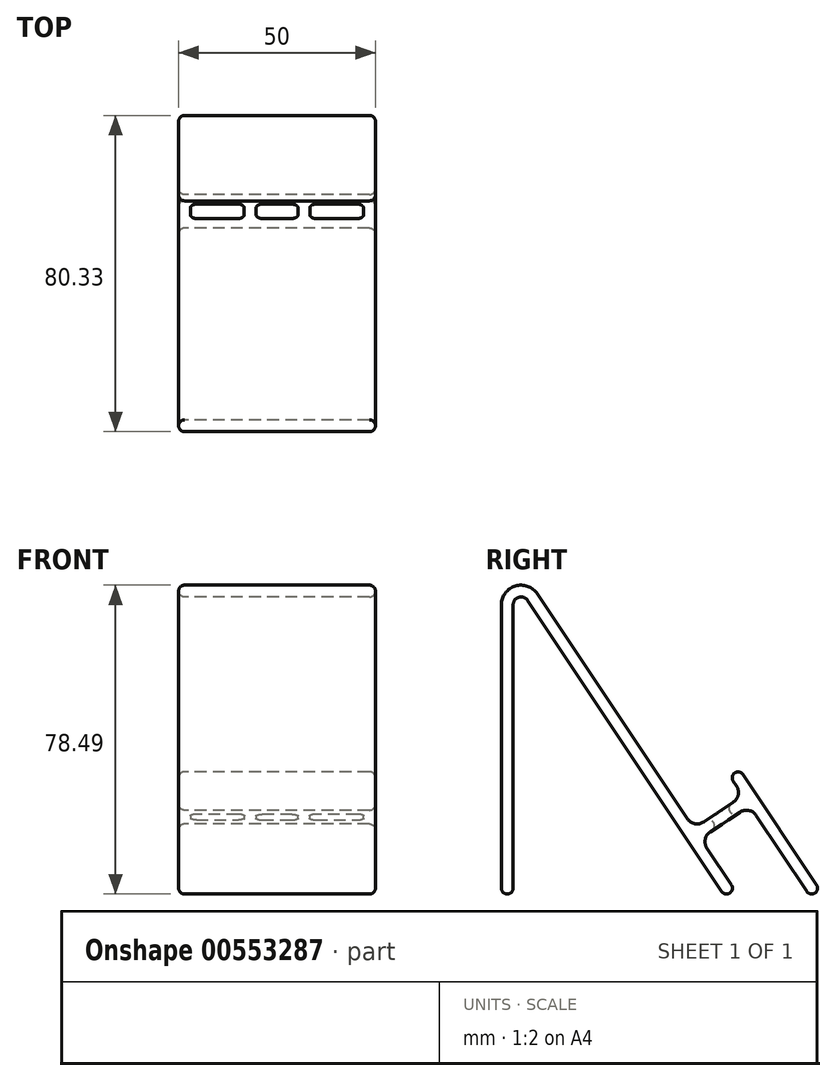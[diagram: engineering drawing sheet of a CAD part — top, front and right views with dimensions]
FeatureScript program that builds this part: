
annotation { "Feature Type Name" : "Feature", "Feature Type Description" : "" }
export const myFeature = defineFeature(function(context is Context, id is Id, definition is map)
    precondition{}
    {
        {
            var Q0;
            Q0=qCreatedBy(makeId("Right.planeOp"),FACE);
            var sketch = newSketch(context, id + "F0", { "sketchPlane" : qUnion([Q0])});
            skLineSegment(sketch, "E0", {"start": v(0, 0) * mm, "end": v(-3.6, 0) * mm});
            skLineSegment(sketch, "E1", {"start": v(-60, 0) * mm, "end": v(-60, 73.49) * mm});
            skLineSegment(sketch, "E2", {"start": v(-50.84, 76.26) * mm, "end": v(-12.76, 19.14) * mm});
            skLineSegment(sketch, "E3", {"start": v(-8.6, 18.3) * mm, "end": v(-1.1, 23.3) * mm});
            skLineSegment(sketch, "E4", {"start": v(-0.28, 27.46) * mm, "end": v(-1.1, 28.7) * mm});
            skLineSegment(sketch, "E5", {"start": v(-0.7, 30.79) * mm, "end": v(-0.7, 30.79) * mm});
            skLineSegment(sketch, "E6", {"start": v(1.39, 30.37) * mm, "end": v(21.63, 0) * mm});
            skLineSegment(sketch, "E7", {"start": v(21.63, 0) * mm, "end": v(18.03, 0) * mm});
            skPoint(sketch, "E8.visualSharp", {"position": v(-60, 90) * mm});
            skArc(sketch, "E8.filletArc", {"start": v(-50.84, 76.26) * mm, "mid": v(-56.45, 78.27) * mm, "end": v(-60, 73.49) * mm});
            skLineSegment(sketch, "E9.0", {"start": v(-53.34, 74.6) * mm, "end": v(-3.6, 0) * mm});
            skArc(sketch, "E9.1", {"start": v(-53.34, 74.6) * mm, "mid": v(-55.58, 75.4) * mm, "end": v(-57, 73.49) * mm});
            skLineSegment(sketch, "E9.2", {"start": v(-57, 0) * mm, "end": v(-57, 73.49) * mm});
            skLineSegment(sketch, "E10.0", {"start": v(-6.93, 15.8) * mm, "end": v(0.55, 20.8) * mm});
            skLineSegment(sketch, "E11", {"start": v(4.71, 19.97) * mm, "end": v(18.03, 0) * mm});
            skLineSegment(sketch, "E12.trimOffspring", {"start": v(-7.77, 11.65) * mm, "end": v(0, 0) * mm});
            skPoint(sketch, "E13.visualSharp", {"position": v(-11.1, 16.64) * mm});
            skArc(sketch, "E13.filletArc", {"start": v(-12.76, 19.14) * mm, "mid": v(-10.85, 17.86) * mm, "end": v(-8.6, 18.3) * mm});
            skPoint(sketch, "E14.visualSharp", {"position": v(1.39, 24.96) * mm});
            skArc(sketch, "E14.filletArc", {"start": v(-1.1, 23.3) * mm, "mid": v(0.17, 25.2) * mm, "end": v(-0.28, 27.46) * mm});
            skPoint(sketch, "E15.visualSharp", {"position": v(3.05, 22.47) * mm});
            skArc(sketch, "E15.filletArc", {"start": v(4.71, 19.97) * mm, "mid": v(2.8, 21.25) * mm, "end": v(0.55, 20.8) * mm});
            skPoint(sketch, "E16.visualSharp", {"position": v(-9.43, 14.14) * mm});
            skArc(sketch, "E16.filletArc", {"start": v(-6.93, 15.8) * mm, "mid": v(-8.21, 13.9) * mm, "end": v(-7.77, 11.65) * mm});
            skLineSegment(sketch, "E17.trimOffspring", {"start": v(-57, 0) * mm, "end": v(-60, 0) * mm});
            skPoint(sketch, "E18.visualSharp", {"position": v(0.55, 31.62) * mm});
            skArc(sketch, "E18.filletArc", {"start": v(1.39, 30.37) * mm, "mid": v(0.43, 31) * mm, "end": v(-0.7, 30.79) * mm});
            skPoint(sketch, "E19.visualSharp", {"position": v(-1.94, 29.95) * mm});
            skArc(sketch, "E19.filletArc", {"start": v(-0.7, 30.79) * mm, "mid": v(-1.33, 29.83) * mm, "end": v(-1.1, 28.7) * mm});
            skSolve(sketch);
        }
        {
            var Q0;
            Q0=makeQuery(id+"F0.imprint","IMPRINT",FACE,{"disambiguationData":[TD([[makeQuery(id+"F0.imprint","IMPRINT",EDGE,{"derivedFrom":sQuery(id+"F0.wireOp",EDGE,"E0")}),-1.0]])]});
            extrude(context, id + "F1", {"entities" : qUnion([Q0]), "endBound" : BoundingType.SYMMETRIC, "depth" : 50 * mm, "offsetDistance" : 25 * mm});
        }
        {
            var Q0;
            Q0=makeQuery(id+"F1.opExtrude","SWEPT_FACE",FACE,{"disambiguationData":[OSD([sQuery(id+"F0.wireOp",EDGE,"E3")])]});
            var sketch = newSketch(context, id + "F2", { "sketchPlane" : qUnion([Q0])});
            skLineSegment(sketch, "E20.0", {"start": v(-23, 10) * mm, "end": v(-23, 5) * mm});
            skLineSegment(sketch, "E20.1", {"start": v(20.5, 10) * mm, "end": v(9.83, 10) * mm});
            skLineSegment(sketch, "E20.2", {"start": v(23, 5) * mm, "end": v(23, 10) * mm});
            skLineSegment(sketch, "E20.3", {"start": v(-20.5, 5) * mm, "end": v(-9.83, 5) * mm});
            skLineSegment(sketch, "E21.0", {"start": v(-22, 8.5) * mm, "end": v(-22, 6.5) * mm});
            skLineSegment(sketch, "E22.0", {"start": v(22, 6.5) * mm, "end": v(22, 8.5) * mm});
            skArc(sketch, "E23.filletArc", {"start": v(20.5, 5) * mm, "mid": v(21.56, 5.44) * mm, "end": v(22, 6.5) * mm});
            skArc(sketch, "E24.filletArc", {"start": v(22, 8.5) * mm, "mid": v(21.56, 9.56) * mm, "end": v(20.5, 10) * mm});
            skArc(sketch, "E25.filletArc", {"start": v(-20.5, 10) * mm, "mid": v(-21.56, 9.56) * mm, "end": v(-22, 8.5) * mm});
            skArc(sketch, "E26.filletArc", {"start": v(-22, 6.5) * mm, "mid": v(-21.56, 5.44) * mm, "end": v(-20.5, 5) * mm});
            skLineSegment(sketch, "E27", {"start": v(-20.5, 5) * mm, "end": v(-20.5, 4) * mm, "construction": true});
            skLineSegment(sketch, "E28", {"start": v(-20.5, 4) * mm, "end": v(-20.5, 3) * mm, "construction": true});
            skLineSegment(sketch, "E29", {"start": v(-20.5, 3) * mm, "end": v(-20.5, 2) * mm, "construction": true});
            skLineSegment(sketch, "E30", {"start": v(-20.5, 2) * mm, "end": v(20.5, 5) * mm, "construction": true});
            skLineSegment(sketch, "E31", {"start": v(-20.5, 3) * mm, "end": v(6.83, 5) * mm, "construction": true});
            skLineSegment(sketch, "E32", {"start": v(-20.5, 4) * mm, "end": v(-6.83, 5) * mm, "construction": true});
            skLineSegment(sketch, "E33", {"start": v(-6.83, 5) * mm, "end": v(-6.83, 10) * mm, "construction": true});
            skLineSegment(sketch, "E34", {"start": v(6.83, 5) * mm, "end": v(6.83, 10) * mm, "construction": true});
            skLineSegment(sketch, "E35.0", {"start": v(8.33, 6.5) * mm, "end": v(8.33, 8.5) * mm});
            skLineSegment(sketch, "E36.0", {"start": v(5.33, 6.5) * mm, "end": v(5.33, 8.5) * mm});
            skLineSegment(sketch, "E37.0", {"start": v(-5.33, 6.5) * mm, "end": v(-5.33, 8.5) * mm});
            skLineSegment(sketch, "E38.0", {"start": v(-8.33, 6.5) * mm, "end": v(-8.33, 8.5) * mm});
            skLineSegment(sketch, "E39.trimOffspring", {"start": v(9.83, 5) * mm, "end": v(20.5, 5) * mm});
            skLineSegment(sketch, "E40.trimOffspring", {"start": v(3.83, 10) * mm, "end": v(-3.83, 10) * mm});
            skLineSegment(sketch, "E41.trimOffspring", {"start": v(-9.83, 10) * mm, "end": v(-20.5, 10) * mm});
            skLineSegment(sketch, "E42.trimOffspring", {"start": v(-3.83, 5) * mm, "end": v(3.83, 5) * mm});
            skPoint(sketch, "E43.visualSharp", {"position": v(8.33, 5) * mm});
            skArc(sketch, "E43.filletArc", {"start": v(8.33, 6.5) * mm, "mid": v(8.77, 5.44) * mm, "end": v(9.83, 5) * mm});
            skPoint(sketch, "E44.visualSharp", {"position": v(8.33, 10) * mm});
            skArc(sketch, "E44.filletArc", {"start": v(9.83, 10) * mm, "mid": v(8.77, 9.56) * mm, "end": v(8.33, 8.5) * mm});
            skArc(sketch, "E45.filletArc", {"start": v(5.33, 8.5) * mm, "mid": v(4.9, 9.56) * mm, "end": v(3.83, 10) * mm});
            skArc(sketch, "E46.filletArc", {"start": v(3.83, 5) * mm, "mid": v(4.9, 5.44) * mm, "end": v(5.33, 6.5) * mm});
            skArc(sketch, "E47.filletArc", {"start": v(-9.83, 5) * mm, "mid": v(-8.77, 5.44) * mm, "end": v(-8.33, 6.5) * mm});
            skArc(sketch, "E48.filletArc", {"start": v(-8.33, 8.5) * mm, "mid": v(-8.77, 9.56) * mm, "end": v(-9.83, 10) * mm});
            skPoint(sketch, "E49.visualSharp", {"position": v(-5.33, 10) * mm});
            skArc(sketch, "E49.filletArc", {"start": v(-3.83, 10) * mm, "mid": v(-4.9, 9.56) * mm, "end": v(-5.33, 8.5) * mm});
            skPoint(sketch, "E50.visualSharp", {"position": v(-5.33, 5) * mm});
            skArc(sketch, "E50.filletArc", {"start": v(-5.33, 6.5) * mm, "mid": v(-4.9, 5.44) * mm, "end": v(-3.83, 5) * mm});
            skSolve(sketch);
        }
        {
            var Q0;
            Q0=makeQuery(id+"F2.imprint","IMPRINT",FACE,{"disambiguationData":[TD([[makeQuery(id+"F2.imprint","IMPRINT",EDGE,{"derivedFrom":sQuery(id+"F2.wireOp",EDGE,"E20.1")}),1.0]])]});
            var Q1;
            Q1=makeQuery(id+"F2.imprint","IMPRINT",FACE,{"disambiguationData":[TD([[makeQuery(id+"F2.imprint","IMPRINT",EDGE,{"derivedFrom":sQuery(id+"F2.wireOp",EDGE,"E36.0")}),1.0]])]});
            var Q2;
            Q2=makeQuery(id+"F2.imprint","IMPRINT",FACE,{"disambiguationData":[TD([[makeQuery(id+"F2.imprint","IMPRINT",EDGE,{"derivedFrom":sQuery(id+"F2.wireOp",EDGE,"E20.3")}),1.0]])]});
            extrude(context, id + "F3", {"entities" : qUnion([Q0, Q1, Q2]), "operationType" : NewBodyOperationType.REMOVE, "endBound" : BoundingType.THROUGH_ALL, "oppositeDirection" : true, "depth" : 25 * mm, "offsetDistance" : 25 * mm});
        }
        {
            var Q0;
            Q0=makeQuery(id+"F1.opExtrude","SWEPT_FACE",FACE,{"disambiguationData":[OSD([sQuery(id+"F0.wireOp",EDGE,"E3")])]});
            var Q1;
            Q1=makeQuery(id+"F1.opExtrude","SWEPT_FACE",FACE,{"disambiguationData":[OSD([sQuery(id+"F0.wireOp",EDGE,"E10.0")])]});
            var Q2;
            Q2=makeQuery(id+"F1.opExtrude","SWEPT_FACE",FACE,{"disambiguationData":[OSD([sQuery(id+"F0.wireOp",EDGE,"E9.0")])]});
            var Q3;
            Q3=makeQuery(id+"F1.opExtrude","SWEPT_FACE",FACE,{"disambiguationData":[OSD([sQuery(id+"F0.wireOp",EDGE,"E0")])]});
            var Q4;
            Q4=makeQuery(id+"F1.opExtrude","SWEPT_FACE",FACE,{"disambiguationData":[OSD([sQuery(id+"F0.wireOp",EDGE,"E7")])]});
            var Q5;
            Q5=makeQuery(id+"F1.opExtrude","SWEPT_FACE",FACE,{"disambiguationData":[OSD([sQuery(id+"F0.wireOp",EDGE,"E17.trimOffspring")])]});
            fillet(context, id + "F4", {"entities" : qUnion([Q0, Q1, Q2, Q3, Q4, Q5]), "radius" : 1.5 * mm, "tangentPropagation" : true, "allowEdgeOverflow" : false});
        }
    });
